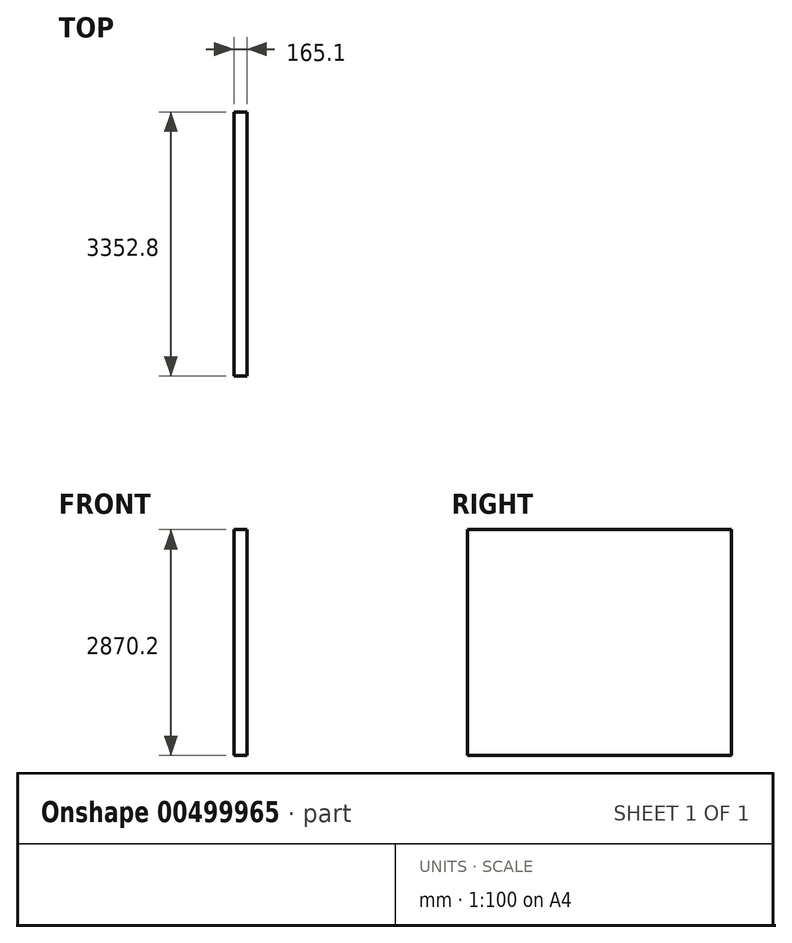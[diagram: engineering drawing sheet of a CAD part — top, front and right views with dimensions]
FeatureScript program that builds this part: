
annotation { "Feature Type Name" : "Feature", "Feature Type Description" : "" }
export const myFeature = defineFeature(function(context is Context, id is Id, definition is map)
    precondition{}
    {
        {
            var Q0;
            Q0=qCreatedBy(makeId("Front.planeOp"),FACE);
            var sketch = newSketch(context, id + "F0", { "sketchPlane" : qUnion([Q0])});
            skLineSegment(sketch, "E0.bottom", {"start": v(-82.55, 1435.1) * mm, "end": v(82.55, 1435.1) * mm});
            skLineSegment(sketch, "E0.top", {"start": v(-82.55, -1435.1) * mm, "end": v(82.55, -1435.1) * mm});
            skLineSegment(sketch, "E0.left", {"start": v(-82.55, 1435.1) * mm, "end": v(-82.55, -1435.1) * mm});
            skLineSegment(sketch, "E0.right", {"start": v(82.55, 1435.1) * mm, "end": v(82.55, -1435.1) * mm});
            skPoint(sketch, "E0.middle", {"position": v(0, 0) * mm});
            skSolve(sketch);
        }
        {
            var Q0;
            Q0 = qSketchRegion(id + "F0", true);
            extrude(context, id + "F1", {"entities" : qUnion([Q0]), "depth" : 3352.8 * mm, "offsetDistance" : 25.4 * mm});
        }
    });
